# Revit family: FU_Inspec_Grade_Plus_2-7
name_source: partatom
category: Furniture
units: mm (PartAtom-declared; Revit-internal decimal feet)

## family parameters
Always vertical = Yes
Cut with Voids When Loaded = No
OmniClass Number = 23.40.20.00
OmniClass Title = General Furniture and Specialties
Room Calculation Point = No
Shared = No
Work Plane-Based = No

## types (2) — shared parameters
Assembly Code = E2020
Depth = 550 mm
Height = 880 mm
Keynote = 46.B
Manufacturer = Inspec
Seat Pad Material = Colour - Khaki
URL = https://inspecfurniture.com
Weight = 7.2 kg
Width = 590 mm
zero-valued in all types: Default Elevation

## per-type parameters (varying)
| type | Description | Frame Material | Model | Seat Material |
| Grade Plus 2.7 - Black - Black | 360° swivel armchair with recycled polypropylene seat on a polished aluminum 4 foot base with optional casters | Metal - Black - Matte | Grade Plus 2.7 | Plastic - Black |
| Grade Plus 2.8 - Chrome - White | 360° swivel armchair with recycled polypropylene seat on a polished aluminum 4 foot base with optional casters. With upholstered seat pad | Metal - Chrome - Polished | Grade Plus 2.8 | Plastic - White |

## geometry (parser evidence)
native form markers: Blend x4, Sweep x2
no freeform markers — native parametric forms only
